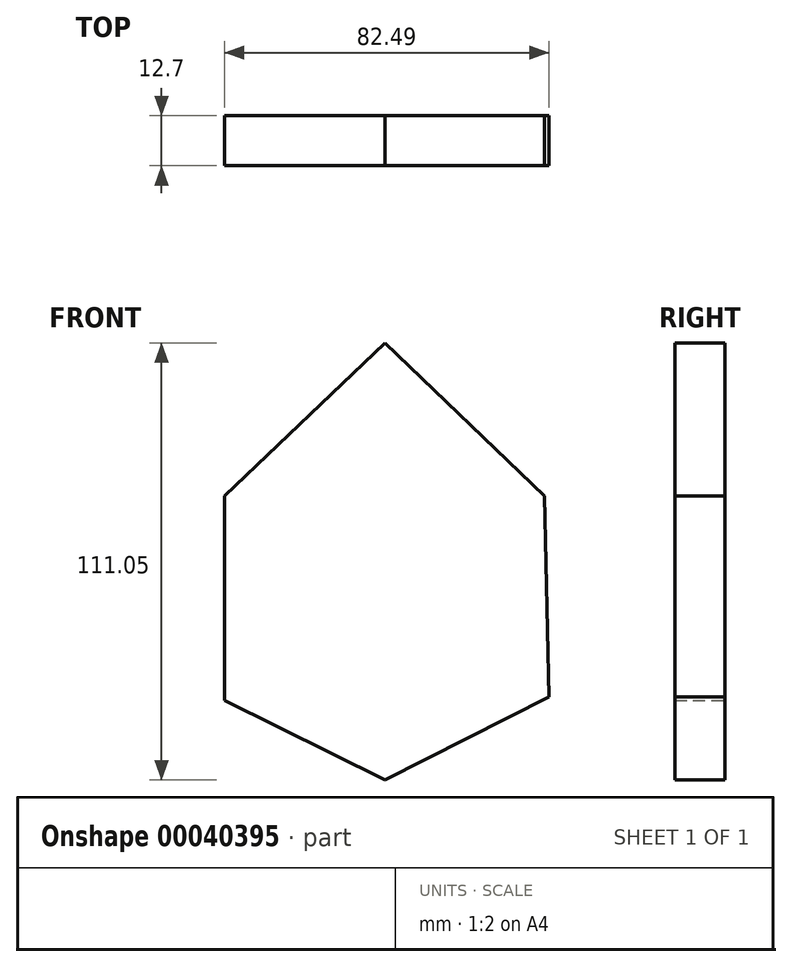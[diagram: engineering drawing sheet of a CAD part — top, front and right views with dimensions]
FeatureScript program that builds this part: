
annotation { "Feature Type Name" : "Feature", "Feature Type Description" : "" }
export const myFeature = defineFeature(function(context is Context, id is Id, definition is map)
    precondition{}
    {
        {
            var Q0;
            Q0=qCreatedBy(makeId("Front.planeOp"),FACE);
            var sketch = newSketch(context, id + "F0", { "sketchPlane" : qUnion([Q0])});
            skLineSegment(sketch, "E0", {"start": v(0, 54.14) * mm, "end": v(-40.85, 15.27) * mm});
            skLineSegment(sketch, "E1", {"start": v(-40.85, 15.27) * mm, "end": v(40.45, 15.27) * mm});
            skLineSegment(sketch, "E2", {"start": v(40.45, 15.27) * mm, "end": v(0, 54.14) * mm});
            skLineSegment(sketch, "E3", {"start": v(-40.85, 15.27) * mm, "end": v(-40.85, -36.69) * mm});
            skLineSegment(sketch, "E4", {"start": v(-40.85, -36.69) * mm, "end": v(0, -56.91) * mm});
            skLineSegment(sketch, "E5", {"start": v(0, -56.91) * mm, "end": v(41.64, -35.9) * mm});
            skLineSegment(sketch, "E6", {"start": v(41.64, -35.9) * mm, "end": v(40.45, 15.27) * mm});
            skSolve(sketch);
        }
        {
            var Q0;
            Q0=makeQuery(id+"F0.imprint","IMPRINT",FACE,{"disambiguationData":[TD([[makeQuery(id+"F0.imprint","IMPRINT",EDGE,{"derivedFrom":sQuery(id+"F0.wireOp",EDGE,"E0")}),1.0]])]});
            var Q1;
            Q1=makeQuery(id+"F0.imprint","IMPRINT",FACE,{"disambiguationData":[TD([[makeQuery(id+"F0.imprint","IMPRINT",EDGE,{"derivedFrom":sQuery(id+"F0.wireOp",EDGE,"E1")}),-1.0]])]});
            extrude(context, id + "F1", {"entities" : qUnion([Q0, Q1]), "depth" : 12.7 * mm});
        }
    });
